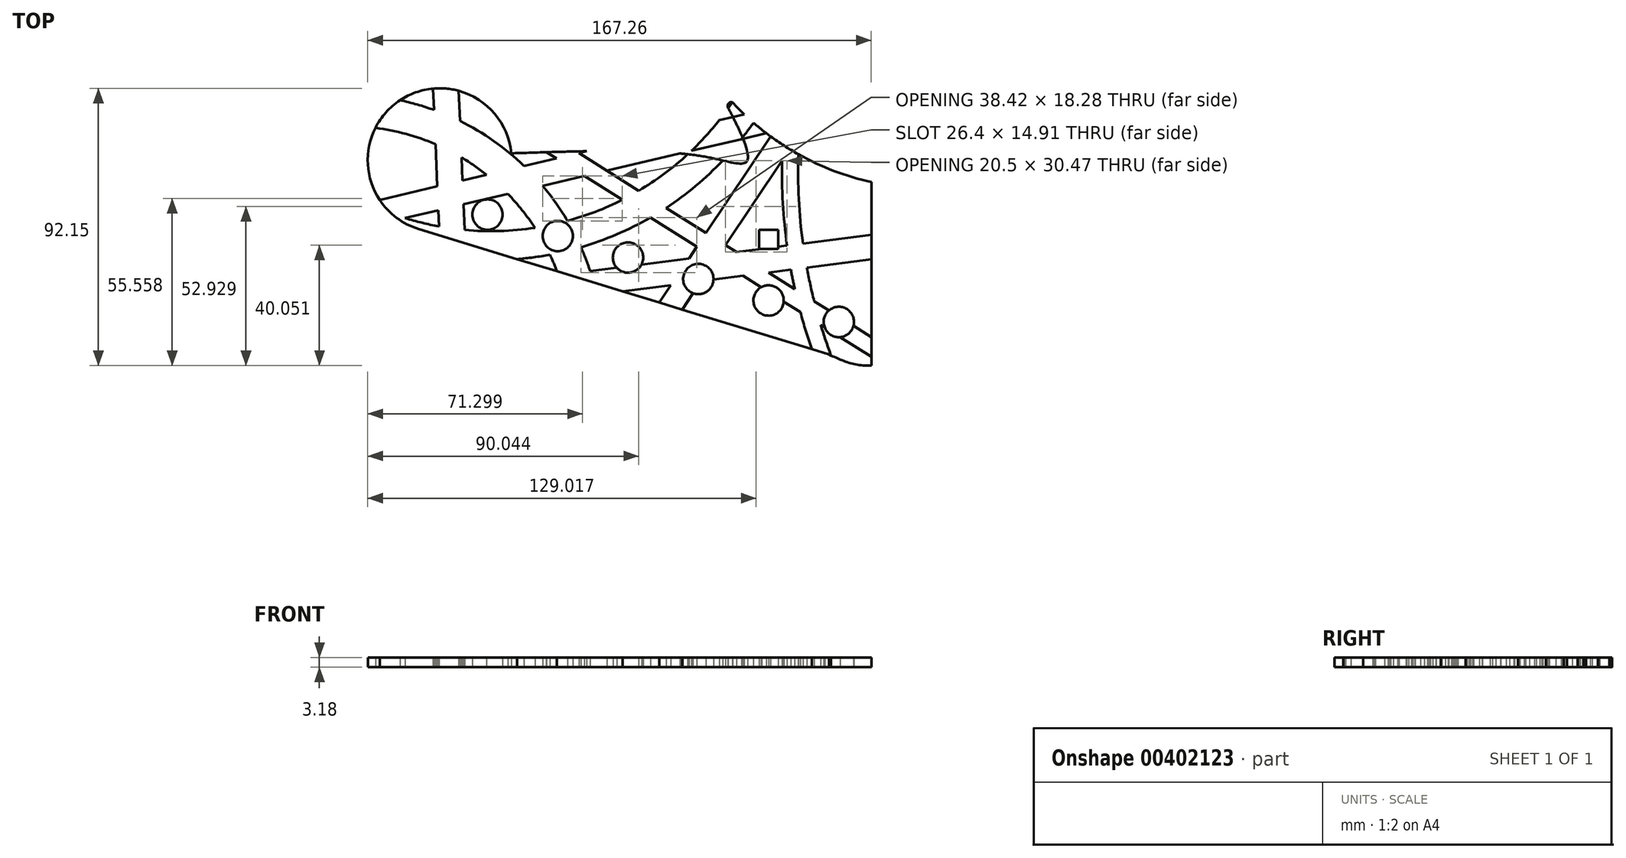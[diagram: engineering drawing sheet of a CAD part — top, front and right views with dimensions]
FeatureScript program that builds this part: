
annotation { "Feature Type Name" : "Feature", "Feature Type Description" : "" }
export const myFeature = defineFeature(function(context is Context, id is Id, definition is map)
    precondition{}
    {
        {
            var Q0;
            Q0=qCreatedBy(makeId("Top.planeOp"),FACE);
            var sketch = newSketch(context, id + "F0", { "sketchPlane" : qUnion([Q0])});
            skArc(sketch, "E0", {"start": v(-90.46, -15.28) * mm, "mid": v(-14.2, -9.68) * mm, "end": v(38.46, 45.77) * mm});
            skArc(sketch, "E1.0", {"start": v(-100.3, -1.2) * mm, "mid": v(-24.88, -3.77) * mm, "end": v(29.26, 48.8) * mm});
            skArc(sketch, "E2", {"start": v(51.31, 64.63) * mm, "mid": v(42.5, 3.49) * mm, "end": v(55.46, -56.9) * mm});
            skArc(sketch, "E3.0", {"start": v(46.25, 66.31) * mm, "mid": v(37.17, 3.3) * mm, "end": v(50.52, -58.93) * mm});
            skArc(sketch, "E4", {"start": v(-33.41, -40.98) * mm, "mid": v(-60.63, 8.15) * mm, "end": v(-114.4, 24.36) * mm});
            skArc(sketch, "E5.0", {"start": v(-23.07, -39.74) * mm, "mid": v(-54.1, 16.25) * mm, "end": v(-115.38, 34.73) * mm});
            skLineSegment(sketch, "E6.0", {"start": v(52.65, -51.2) * mm, "end": v(-83.61, -9.54) * mm});
            skArc(sketch, "E6.1", {"start": v(-52.83, 15.6) * mm, "mid": v(-91.75, 31.83) * mm, "end": v(-83.61, -9.54) * mm});
            skFitSpline(sketch, "E6.5", {"points": [v(52.65, -51.2) * mm, v(64.8, -54.91) * mm, v(80.38, -50.62) * mm, v(85.15, -44.27) * mm]});
            skLineSegment(sketch, "E6.6", {"start": v(66.1, 6.22) * mm, "end": v(66.1, -52.4) * mm});
            skPoint(sketch, "E7.visualSharp", {"position": v(13.9, 42.17) * mm});
            skArc(sketch, "E8", {"start": v(12.87, 42.18) * mm, "mid": v(44.36, 14.28) * mm, "end": v(85.15, 3.99) * mm});
            skFitSpline(sketch, "E9", {"points": [v(-52.83, 15.6) * mm, v(12.87, 42.18) * mm], "startDerivative": vector(194.61, -3.65) * mm, "endDerivative": vector(-37.72, 87.36) * mm});
            skLineSegment(sketch, "E10", {"start": v(66.73, 6.07) * mm, "end": v(66.73, -50.68) * mm});
            skLineSegment(sketch, "E11", {"start": v(66.73, -50.68) * mm, "end": v(66.73, -55.63) * mm});
            skArc(sketch, "E12", {"start": v(66.1, -52.4) * mm, "mid": v(66.43, -52.34) * mm, "end": v(66.73, -52.2) * mm});
            skSolve(sketch);
        }
        {
            var Q0;
            Q0=qCreatedBy(makeId("Top.planeOp"),FACE);
            var sketch = newSketch(context, id + "F1", { "sketchPlane" : qUnion([Q0])});
            skLineSegment(sketch, "E13", {"start": v(41.28, 19.45) * mm, "end": v(0, -42.12) * mm});
            skLineSegment(sketch, "E14", {"start": v(0, -42.12) * mm, "end": v(-6.32, -37.88) * mm});
            skLineSegment(sketch, "E15", {"start": v(-6.32, -37.88) * mm, "end": v(38.05, 28.32) * mm});
            skLineSegment(sketch, "E16", {"start": v(38.05, 28.32) * mm, "end": v(41.28, 19.45) * mm});
            skLineSegment(sketch, "E17", {"start": v(40.9, -75.03) * mm, "end": v(46.22, -72.68) * mm});
            skLineSegment(sketch, "E18", {"start": v(-56.42, -35.5) * mm, "end": v(132.52, -11.1) * mm});
            skLineSegment(sketch, "E19", {"start": v(132.52, -11.1) * mm, "end": v(131.24, -3.12) * mm});
            skLineSegment(sketch, "E20", {"start": v(131.24, -3.12) * mm, "end": v(-56.79, -27.4) * mm});
            skLineSegment(sketch, "E21", {"start": v(-56.79, -27.4) * mm, "end": v(-56.42, -35.5) * mm});
            skLineSegment(sketch, "E22", {"start": v(-71.95, 73.85) * mm, "end": v(-66.69, -48.5) * mm});
            skLineSegment(sketch, "E23", {"start": v(-66.69, -48.5) * mm, "end": v(-75.13, -48.86) * mm});
            skLineSegment(sketch, "E24", {"start": v(-75.13, -48.86) * mm, "end": v(-80.24, 69.83) * mm});
            skLineSegment(sketch, "E25", {"start": v(-80.24, 69.83) * mm, "end": v(-71.95, 73.85) * mm});
            skLineSegment(sketch, "E26", {"start": v(70.66, -54.45) * mm, "end": v(-45.44, 18.7) * mm});
            skLineSegment(sketch, "E27", {"start": v(-45.44, 18.7) * mm, "end": v(-42.5, 23.35) * mm});
            skLineSegment(sketch, "E28", {"start": v(-42.5, 23.35) * mm, "end": v(73.52, -49.75) * mm});
            skLineSegment(sketch, "E29", {"start": v(73.52, -49.75) * mm, "end": v(70.66, -54.45) * mm});
            skLineSegment(sketch, "E30", {"start": v(56.6, 28.12) * mm, "end": v(-113.4, -11.85) * mm});
            skLineSegment(sketch, "E31", {"start": v(-113.4, -11.85) * mm, "end": v(-115.19, -4.23) * mm});
            skLineSegment(sketch, "E32", {"start": v(-115.19, -4.23) * mm, "end": v(55.1, 35.8) * mm});
            skLineSegment(sketch, "E33", {"start": v(55.1, 35.8) * mm, "end": v(56.6, 28.12) * mm});
            skArc(sketch, "E34.0", {"start": v(-90.46, -15.28) * mm, "mid": v(-14.2, -9.68) * mm, "end": v(38.46, 45.77) * mm});
            skArc(sketch, "E34.1", {"start": v(-100.3, -1.2) * mm, "mid": v(-24.88, -3.77) * mm, "end": v(29.26, 48.8) * mm});
            skArc(sketch, "E34.2", {"start": v(51.31, 64.63) * mm, "mid": v(42.5, 3.49) * mm, "end": v(55.46, -56.9) * mm});
            skArc(sketch, "E34.3", {"start": v(46.25, 66.31) * mm, "mid": v(37.17, 3.3) * mm, "end": v(50.52, -58.93) * mm});
            skArc(sketch, "E34.4", {"start": v(-33.41, -40.98) * mm, "mid": v(-60.63, 8.15) * mm, "end": v(-114.4, 24.36) * mm});
            skArc(sketch, "E34.5", {"start": v(-23.07, -39.74) * mm, "mid": v(-54.1, 16.25) * mm, "end": v(-115.38, 34.73) * mm});
            skArc(sketch, "E35.0", {"start": v(-52.83, 15.6) * mm, "mid": v(-91.75, 31.83) * mm, "end": v(-83.61, -9.54) * mm});
            skFitSpline(sketch, "E35.1", {"points": [v(-52.83, 15.6) * mm, v(12.04, 14.39) * mm, v(25.44, 13.06) * mm, v(12.87, 42.18) * mm]});
            skArc(sketch, "E35.2", {"start": v(12.87, 42.18) * mm, "mid": v(44.36, 14.28) * mm, "end": v(85.15, 3.99) * mm});
            skLineSegment(sketch, "E35.3", {"start": v(66.1, 6.22) * mm, "end": v(66.1, -52.4) * mm});
            skFitSpline(sketch, "E35.4", {"points": [v(52.65, -51.2) * mm, v(64.8, -54.91) * mm, v(80.38, -50.62) * mm, v(85.15, -44.27) * mm]});
            skLineSegment(sketch, "E35.5", {"start": v(52.65, -51.2) * mm, "end": v(-83.61, -9.54) * mm});
            skLineSegment(sketch, "E36.0", {"start": v(66.73, 6.07) * mm, "end": v(66.73, -50.68) * mm});
            skLineSegment(sketch, "E37.0", {"start": v(66.73, -50.68) * mm, "end": v(66.73, -55.63) * mm});
            skArc(sketch, "E38.0", {"start": v(66.1, -52.4) * mm, "mid": v(66.43, -52.34) * mm, "end": v(66.73, -52.2) * mm});
            skSolve(sketch);
        }
        {
            var Q0;
            {var subQ0=sQuery(id+"F1.wireOp",EDGE,"E35.3");var subQ1=sQuery(id+"F1.wireOp",EDGE,"E26");var subQ2=makeQuery(id+"F1.imprint","INTERSECT",VERTEX,{"derivedFrom":[subQ1,subQ0]});Q0=makeQuery(id+"F1.imprint","IMPRINT",FACE,{"disambiguationData":[TD([[makeQuery(id+"F1.imprint","IMPRINT",EDGE,{"disambiguationData":[TD([[subQ2,-1.0]])],"derivedFrom":subQ1}),-1.0]])]});}
            var Q1;
            {var subQ0=sQuery(id+"F1.wireOp",EDGE,"E37.0");var subQ6=sQuery(id+"F1.wireOp",EDGE,"E26");var subQ9=makeQuery(id+"F1.imprint","INTERSECT",VERTEX,{"derivedFrom":[subQ6,subQ0]});Q1=makeQuery(id+"F1.imprint","IMPRINT",FACE,{"disambiguationData":[TD([[makeQuery(id+"F1.imprint","IMPRINT",EDGE,{"disambiguationData":[TD([[subQ9,-1.0]])],"derivedFrom":subQ6}),-1.0]])]});}
            var Q2;
            {var subQ0=sQuery(id+"F1.wireOp",EDGE,"E36.0");var subQ1=sQuery(id+"F1.wireOp",EDGE,"E18");var subQ2=makeQuery(id+"F1.imprint","INTERSECT",VERTEX,{"derivedFrom":[subQ1,subQ0]});Q2=makeQuery(id+"F1.imprint","IMPRINT",FACE,{"disambiguationData":[TD([[makeQuery(id+"F1.imprint","IMPRINT",EDGE,{"disambiguationData":[TD([[subQ2,1.0]])],"derivedFrom":subQ1}),1.0]])]});}
            var Q3;
            {var subQ0=sQuery(id+"F1.wireOp",EDGE,"E34.2");var subQ1=sQuery(id+"F1.wireOp",EDGE,"E18");var subQ2=makeQuery(id+"F1.imprint","INTERSECT",VERTEX,{"derivedFrom":[subQ1,subQ0]});Q3=makeQuery(id+"F1.imprint","IMPRINT",FACE,{"disambiguationData":[TD([[makeQuery(id+"F1.imprint","IMPRINT",EDGE,{"disambiguationData":[TD([[subQ2,-1.0]])],"derivedFrom":subQ1}),1.0]])]});}
            var Q4;
            {var subQ0=sQuery(id+"F1.wireOp",EDGE,"E34.2");var subQ1=sQuery(id+"F1.wireOp",EDGE,"E13");var subQ2=makeQuery(id+"F1.imprint","INTERSECT",VERTEX,{"derivedFrom":[subQ1,subQ0]});Q4=makeQuery(id+"F1.imprint","IMPRINT",FACE,{"disambiguationData":[TD([[makeQuery(id+"F1.imprint","IMPRINT",EDGE,{"disambiguationData":[TD([[subQ2,-1.0]])],"derivedFrom":subQ1}),-1.0]])]});}
            var Q5;
            {var subQ0=sQuery(id+"F1.wireOp",EDGE,"E34.3");var subQ1=sQuery(id+"F1.wireOp",EDGE,"E13");var subQ2=makeQuery(id+"F1.imprint","INTERSECT",VERTEX,{"derivedFrom":[subQ1,subQ0]});Q5=makeQuery(id+"F1.imprint","IMPRINT",FACE,{"disambiguationData":[TD([[makeQuery(id+"F1.imprint","IMPRINT",EDGE,{"disambiguationData":[TD([[subQ2,-1.0]])],"derivedFrom":subQ1}),-1.0]])]});}
            var Q6;
            {var subQ0=sQuery(id+"F1.wireOp",EDGE,"E34.2");var subQ1=sQuery(id+"F1.wireOp",EDGE,"E13");var subQ2=makeQuery(id+"F1.imprint","INTERSECT",VERTEX,{"derivedFrom":[subQ1,subQ0]});Q6=makeQuery(id+"F1.imprint","IMPRINT",FACE,{"disambiguationData":[TD([[makeQuery(id+"F1.imprint","IMPRINT",EDGE,{"disambiguationData":[TD([[subQ2,-1.0]])],"derivedFrom":subQ1}),1.0]])]});}
            var Q7;
            {var subQ0=sQuery(id+"F1.wireOp",EDGE,"E34.3");var subQ1=sQuery(id+"F1.wireOp",EDGE,"E18");var subQ2=makeQuery(id+"F1.imprint","INTERSECT",VERTEX,{"derivedFrom":[subQ1,subQ0]});Q7=makeQuery(id+"F1.imprint","IMPRINT",FACE,{"disambiguationData":[TD([[makeQuery(id+"F1.imprint","IMPRINT",EDGE,{"disambiguationData":[TD([[subQ2,-1.0]])],"derivedFrom":subQ1}),1.0]])]});}
            var Q8;
            {var subQ0=sQuery(id+"F1.wireOp",EDGE,"E34.3");var subQ1=sQuery(id+"F1.wireOp",EDGE,"E18");var subQ2=makeQuery(id+"F1.imprint","INTERSECT",VERTEX,{"derivedFrom":[subQ1,subQ0]});Q8=makeQuery(id+"F1.imprint","IMPRINT",FACE,{"disambiguationData":[TD([[makeQuery(id+"F1.imprint","IMPRINT",EDGE,{"disambiguationData":[TD([[subQ2,-1.0]])],"derivedFrom":subQ1}),-1.0]])]});}
            var Q9;
            {var subQ0=sQuery(id+"F1.wireOp",EDGE,"E34.2");var subQ1=sQuery(id+"F1.wireOp",EDGE,"E26");var subQ2=makeQuery(id+"F1.imprint","INTERSECT",VERTEX,{"derivedFrom":[subQ1,subQ0]});Q9=makeQuery(id+"F1.imprint","IMPRINT",FACE,{"disambiguationData":[TD([[makeQuery(id+"F1.imprint","IMPRINT",EDGE,{"disambiguationData":[TD([[subQ2,-1.0]])],"derivedFrom":subQ1}),-1.0]])]});}
            var Q10;
            {var subQ3=sQuery(id+"F1.wireOp",EDGE,"E34.2");var subQ7=sQuery(id+"F1.wireOp",EDGE,"E26");var subQ9=makeQuery(id+"F1.imprint","INTERSECT",VERTEX,{"derivedFrom":[subQ7,subQ3]});Q10=makeQuery(id+"F1.imprint","IMPRINT",FACE,{"disambiguationData":[TD([[makeQuery(id+"F1.imprint","IMPRINT",EDGE,{"disambiguationData":[TD([[subQ9,-1.0]])],"derivedFrom":subQ7}),1.0]])]});}
            var Q11;
            {var subQ0=sQuery(id+"F1.wireOp",EDGE,"E26");var subQ1=sQuery(id+"F1.wireOp",EDGE,"E18");var subQ2=makeQuery(id+"F1.imprint","INTERSECT",VERTEX,{"derivedFrom":[subQ1,subQ0]});Q11=makeQuery(id+"F1.imprint","IMPRINT",FACE,{"disambiguationData":[TD([[makeQuery(id+"F1.imprint","IMPRINT",EDGE,{"disambiguationData":[TD([[subQ2,-1.0]])],"derivedFrom":subQ1}),-1.0]])]});}
            var Q12;
            {var subQ0=sQuery(id+"F1.wireOp",EDGE,"E28");var subQ1=sQuery(id+"F1.wireOp",EDGE,"E18");var subQ2=makeQuery(id+"F1.imprint","INTERSECT",VERTEX,{"derivedFrom":[subQ1,subQ0]});Q12=makeQuery(id+"F1.imprint","IMPRINT",FACE,{"disambiguationData":[TD([[makeQuery(id+"F1.imprint","IMPRINT",EDGE,{"disambiguationData":[TD([[subQ2,-1.0]])],"derivedFrom":subQ1}),1.0]])]});}
            var Q13;
            {var subQ0=sQuery(id+"F1.wireOp",EDGE,"E20");var subQ1=sQuery(id+"F1.wireOp",EDGE,"E13");var subQ2=makeQuery(id+"F1.imprint","INTERSECT",VERTEX,{"derivedFrom":[subQ1,subQ0]});Q13=makeQuery(id+"F1.imprint","IMPRINT",FACE,{"disambiguationData":[TD([[makeQuery(id+"F1.imprint","IMPRINT",EDGE,{"disambiguationData":[TD([[subQ2,-1.0]])],"derivedFrom":subQ1}),1.0]])]});}
            var Q14;
            {var subQ0=sQuery(id+"F1.wireOp",EDGE,"E28");var subQ1=sQuery(id+"F1.wireOp",EDGE,"E13");var subQ2=makeQuery(id+"F1.imprint","INTERSECT",VERTEX,{"derivedFrom":[subQ1,subQ0]});Q14=makeQuery(id+"F1.imprint","IMPRINT",FACE,{"disambiguationData":[TD([[makeQuery(id+"F1.imprint","IMPRINT",EDGE,{"disambiguationData":[TD([[subQ2,-1.0]])],"derivedFrom":subQ1}),1.0]])]});}
            var Q15;
            {var subQ1=sQuery(id+"F1.wireOp",EDGE,"E13");var subQ7=sQuery(id+"F1.wireOp",EDGE,"E28");var subQ9=makeQuery(id+"F1.imprint","INTERSECT",VERTEX,{"derivedFrom":[subQ1,subQ7]});Q15=makeQuery(id+"F1.imprint","IMPRINT",FACE,{"disambiguationData":[TD([[makeQuery(id+"F1.imprint","IMPRINT",EDGE,{"disambiguationData":[TD([[subQ9,-1.0]])],"derivedFrom":subQ1}),-1.0]])]});}
            var Q16;
            {var subQ0=sQuery(id+"F1.wireOp",EDGE,"E26");var subQ1=sQuery(id+"F1.wireOp",EDGE,"E13");var subQ2=makeQuery(id+"F1.imprint","INTERSECT",VERTEX,{"derivedFrom":[subQ1,subQ0]});Q16=makeQuery(id+"F1.imprint","IMPRINT",FACE,{"disambiguationData":[TD([[makeQuery(id+"F1.imprint","IMPRINT",EDGE,{"disambiguationData":[TD([[subQ2,-1.0]])],"derivedFrom":subQ1}),1.0]])]});}
            var Q17;
            {var subQ0=sQuery(id+"F1.wireOp",EDGE,"E20");var subQ1=sQuery(id+"F1.wireOp",EDGE,"E13");var subQ2=makeQuery(id+"F1.imprint","INTERSECT",VERTEX,{"derivedFrom":[subQ1,subQ0]});Q17=makeQuery(id+"F1.imprint","IMPRINT",FACE,{"disambiguationData":[TD([[makeQuery(id+"F1.imprint","IMPRINT",EDGE,{"disambiguationData":[TD([[subQ2,-1.0]])],"derivedFrom":subQ1}),-1.0]])]});}
            var Q18;
            {var subQ1=sQuery(id+"F1.wireOp",EDGE,"E13");var subQ7=sQuery(id+"F1.wireOp",EDGE,"E26");var subQ9=makeQuery(id+"F1.imprint","INTERSECT",VERTEX,{"derivedFrom":[subQ1,subQ7]});Q18=makeQuery(id+"F1.imprint","IMPRINT",FACE,{"disambiguationData":[TD([[makeQuery(id+"F1.imprint","IMPRINT",EDGE,{"disambiguationData":[TD([[subQ9,-1.0]])],"derivedFrom":subQ1}),-1.0]])]});}
            var Q19;
            {var subQ0=sQuery(id+"F1.wireOp",EDGE,"E20");var subQ1=sQuery(id+"F1.wireOp",EDGE,"E15");var subQ2=makeQuery(id+"F1.imprint","INTERSECT",VERTEX,{"derivedFrom":[subQ1,subQ0]});Q19=makeQuery(id+"F1.imprint","IMPRINT",FACE,{"disambiguationData":[TD([[makeQuery(id+"F1.imprint","IMPRINT",EDGE,{"disambiguationData":[TD([[subQ2,-1.0]])],"derivedFrom":subQ1}),-1.0]])]});}
            var Q20;
            {var subQ0=sQuery(id+"F1.wireOp",EDGE,"E35.5");var subQ1=sQuery(id+"F1.wireOp",EDGE,"E13");var subQ2=makeQuery(id+"F1.imprint","INTERSECT",VERTEX,{"derivedFrom":[subQ1,subQ0]});Q20=makeQuery(id+"F1.imprint","IMPRINT",FACE,{"disambiguationData":[TD([[makeQuery(id+"F1.imprint","IMPRINT",EDGE,{"disambiguationData":[TD([[subQ2,1.0]])],"derivedFrom":subQ1}),-1.0]])]});}
            var Q21;
            {var subQ1=sQuery(id+"F1.wireOp",EDGE,"E18");var subQ3=sQuery(id+"F1.wireOp",EDGE,"E15");var subQ4=makeQuery(id+"F1.imprint","INTERSECT",VERTEX,{"derivedFrom":[subQ3,subQ1]});Q21=makeQuery(id+"F1.imprint","IMPRINT",FACE,{"disambiguationData":[TD([[makeQuery(id+"F1.imprint","IMPRINT",EDGE,{"disambiguationData":[TD([[subQ4,-1.0]])],"derivedFrom":subQ3}),1.0]])]});}
            var Q22;
            {var subQ0=sQuery(id+"F1.wireOp",EDGE,"E26");var subQ1=sQuery(id+"F1.wireOp",EDGE,"E15");var subQ2=makeQuery(id+"F1.imprint","INTERSECT",VERTEX,{"derivedFrom":[subQ1,subQ0]});Q22=makeQuery(id+"F1.imprint","IMPRINT",FACE,{"disambiguationData":[TD([[makeQuery(id+"F1.imprint","IMPRINT",EDGE,{"disambiguationData":[TD([[subQ2,-1.0]])],"derivedFrom":subQ1}),1.0]])]});}
            var Q23;
            {var subQ0=sQuery(id+"F1.wireOp",EDGE,"E34.1");var subQ1=sQuery(id+"F1.wireOp",EDGE,"E28");var subQ2=makeQuery(id+"F1.imprint","INTERSECT",VERTEX,{"derivedFrom":[subQ1,subQ0]});Q23=makeQuery(id+"F1.imprint","IMPRINT",FACE,{"disambiguationData":[TD([[makeQuery(id+"F1.imprint","IMPRINT",EDGE,{"disambiguationData":[TD([[subQ2,-1.0]])],"derivedFrom":subQ1}),1.0]])]});}
            var Q24;
            {var subQ1=sQuery(id+"F1.wireOp",EDGE,"E30");var subQ9=sQuery(id+"F1.wireOp",EDGE,"E34.0");var subQ10=makeQuery(id+"F1.imprint","INTERSECT",VERTEX,{"derivedFrom":[subQ1,subQ9]});Q24=makeQuery(id+"F1.imprint","IMPRINT",FACE,{"disambiguationData":[TD([[makeQuery(id+"F1.imprint","IMPRINT",EDGE,{"disambiguationData":[TD([[subQ10,-1.0]])],"derivedFrom":subQ1}),-1.0]])]});}
            var Q25;
            {var subQ0=sQuery(id+"F1.wireOp",EDGE,"E35.2");var subQ1=sQuery(id+"F1.wireOp",EDGE,"E32");var subQ2=makeQuery(id+"F1.imprint","INTERSECT",VERTEX,{"derivedFrom":[subQ1,subQ0]});Q25=makeQuery(id+"F1.imprint","IMPRINT",FACE,{"disambiguationData":[TD([[makeQuery(id+"F1.imprint","IMPRINT",EDGE,{"disambiguationData":[TD([[subQ2,1.0]])],"derivedFrom":subQ1}),1.0]])]});}
            var Q26;
            {var subQ0=sQuery(id+"F1.wireOp",EDGE,"E35.1");var subQ1=sQuery(id+"F1.wireOp",EDGE,"E28");var subQ2=makeQuery(id+"F1.imprint","INTERSECT",VERTEX,{"derivedFrom":[subQ1,subQ0]});Q26=makeQuery(id+"F1.imprint","IMPRINT",FACE,{"disambiguationData":[TD([[makeQuery(id+"F1.imprint","IMPRINT",EDGE,{"disambiguationData":[TD([[subQ2,-1.0]])],"derivedFrom":subQ1}),1.0]])]});}
            var Q27;
            {var subQ0=sQuery(id+"F1.wireOp",EDGE,"E34.0");var subQ1=sQuery(id+"F1.wireOp",EDGE,"E26");var subQ2=makeQuery(id+"F1.imprint","INTERSECT",VERTEX,{"derivedFrom":[subQ1,subQ0]});Q27=makeQuery(id+"F1.imprint","IMPRINT",FACE,{"disambiguationData":[TD([[makeQuery(id+"F1.imprint","IMPRINT",EDGE,{"disambiguationData":[TD([[subQ2,-1.0]])],"derivedFrom":subQ1}),-1.0]])]});}
            var Q28;
            {var subQ0=sQuery(id+"F1.wireOp",EDGE,"E34.1");var subQ1=sQuery(id+"F1.wireOp",EDGE,"E26");var subQ2=makeQuery(id+"F1.imprint","INTERSECT",VERTEX,{"derivedFrom":[subQ1,subQ0]});Q28=makeQuery(id+"F1.imprint","IMPRINT",FACE,{"disambiguationData":[TD([[makeQuery(id+"F1.imprint","IMPRINT",EDGE,{"disambiguationData":[TD([[subQ2,-1.0]])],"derivedFrom":subQ1}),-1.0]])]});}
            var Q29;
            {var subQ0=sQuery(id+"F1.wireOp",EDGE,"E30");var subQ1=sQuery(id+"F1.wireOp",EDGE,"E26");var subQ2=makeQuery(id+"F1.imprint","INTERSECT",VERTEX,{"derivedFrom":[subQ1,subQ0]});Q29=makeQuery(id+"F1.imprint","IMPRINT",FACE,{"disambiguationData":[TD([[makeQuery(id+"F1.imprint","IMPRINT",EDGE,{"disambiguationData":[TD([[subQ2,-1.0]])],"derivedFrom":subQ1}),-1.0]])]});}
            var Q30;
            {var subQ0=sQuery(id+"F1.wireOp",EDGE,"E35.1");var subQ1=sQuery(id+"F1.wireOp",EDGE,"E26");var subQ2=makeQuery(id+"F1.imprint","INTERSECT",VERTEX,{"derivedFrom":[subQ1,subQ0]});Q30=makeQuery(id+"F1.imprint","IMPRINT",FACE,{"disambiguationData":[TD([[makeQuery(id+"F1.imprint","IMPRINT",EDGE,{"disambiguationData":[TD([[subQ2,1.0]])],"derivedFrom":subQ1}),-1.0]])]});}
            var Q31;
            {var subQ0=sQuery(id+"F1.wireOp",EDGE,"E30");var subQ1=sQuery(id+"F1.wireOp",EDGE,"E26");var subQ2=makeQuery(id+"F1.imprint","INTERSECT",VERTEX,{"derivedFrom":[subQ1,subQ0]});Q31=makeQuery(id+"F1.imprint","IMPRINT",FACE,{"disambiguationData":[TD([[makeQuery(id+"F1.imprint","IMPRINT",EDGE,{"disambiguationData":[TD([[subQ2,-1.0]])],"derivedFrom":subQ1}),1.0]])]});}
            var Q32;
            {var subQ0=sQuery(id+"F1.wireOp",EDGE,"E34.0");var subQ1=sQuery(id+"F1.wireOp",EDGE,"E26");var subQ2=makeQuery(id+"F1.imprint","INTERSECT",VERTEX,{"derivedFrom":[subQ1,subQ0]});Q32=makeQuery(id+"F1.imprint","IMPRINT",FACE,{"disambiguationData":[TD([[makeQuery(id+"F1.imprint","IMPRINT",EDGE,{"disambiguationData":[TD([[subQ2,-1.0]])],"derivedFrom":subQ1}),1.0]])]});}
            var Q33;
            {var subQ0=sQuery(id+"F1.wireOp",EDGE,"E34.5");var subQ1=sQuery(id+"F1.wireOp",EDGE,"E20");var subQ2=makeQuery(id+"F1.imprint","INTERSECT",VERTEX,{"derivedFrom":[subQ1,subQ0]});Q33=makeQuery(id+"F1.imprint","IMPRINT",FACE,{"disambiguationData":[TD([[makeQuery(id+"F1.imprint","IMPRINT",EDGE,{"disambiguationData":[TD([[subQ2,-1.0]])],"derivedFrom":subQ1}),1.0]])]});}
            var Q34;
            {var subQ5=sQuery(id+"F1.wireOp",EDGE,"E34.5");var subQ7=sQuery(id+"F1.wireOp",EDGE,"E20");var subQ8=makeQuery(id+"F1.imprint","INTERSECT",VERTEX,{"derivedFrom":[subQ7,subQ5]});Q34=makeQuery(id+"F1.imprint","IMPRINT",FACE,{"disambiguationData":[TD([[makeQuery(id+"F1.imprint","IMPRINT",EDGE,{"disambiguationData":[TD([[subQ8,-1.0]])],"derivedFrom":subQ7}),-1.0]])]});}
            var Q35;
            {var subQ0=sQuery(id+"F1.wireOp",EDGE,"E34.4");var subQ1=sQuery(id+"F1.wireOp",EDGE,"E34.0");var subQ2=makeQuery(id+"F1.imprint","INTERSECT",VERTEX,{"derivedFrom":[subQ1,subQ0]});Q35=makeQuery(id+"F1.imprint","IMPRINT",FACE,{"disambiguationData":[TD([[makeQuery(id+"F1.imprint","IMPRINT",EDGE,{"disambiguationData":[TD([[subQ2,-1.0]])],"derivedFrom":subQ1}),1.0]])]});}
            var Q36;
            {var subQ0=sQuery(id+"F1.wireOp",EDGE,"E34.5");var subQ1=sQuery(id+"F1.wireOp",EDGE,"E30");var subQ2=makeQuery(id+"F1.imprint","INTERSECT",VERTEX,{"derivedFrom":[subQ1,subQ0]});Q36=makeQuery(id+"F1.imprint","IMPRINT",FACE,{"disambiguationData":[TD([[makeQuery(id+"F1.imprint","IMPRINT",EDGE,{"disambiguationData":[TD([[subQ2,-1.0]])],"derivedFrom":subQ1}),1.0]])]});}
            var Q37;
            {var subQ0=sQuery(id+"F1.wireOp",EDGE,"E34.5");var subQ1=sQuery(id+"F1.wireOp",EDGE,"E30");var subQ2=makeQuery(id+"F1.imprint","INTERSECT",VERTEX,{"derivedFrom":[subQ1,subQ0]});Q37=makeQuery(id+"F1.imprint","IMPRINT",FACE,{"disambiguationData":[TD([[makeQuery(id+"F1.imprint","IMPRINT",EDGE,{"disambiguationData":[TD([[subQ2,-1.0]])],"derivedFrom":subQ1}),-1.0]])]});}
            var Q38;
            {var subQ0=sQuery(id+"F1.wireOp",EDGE,"E34.5");var subQ1=sQuery(id+"F1.wireOp",EDGE,"E22");var subQ2=makeQuery(id+"F1.imprint","INTERSECT",VERTEX,{"derivedFrom":[subQ1,subQ0]});Q38=makeQuery(id+"F1.imprint","IMPRINT",FACE,{"disambiguationData":[TD([[makeQuery(id+"F1.imprint","IMPRINT",EDGE,{"disambiguationData":[TD([[subQ2,-1.0]])],"derivedFrom":subQ1}),1.0]])]});}
            var Q39;
            {var subQ0=sQuery(id+"F1.wireOp",EDGE,"E34.5");var subQ1=sQuery(id+"F1.wireOp",EDGE,"E22");var subQ2=makeQuery(id+"F1.imprint","INTERSECT",VERTEX,{"derivedFrom":[subQ1,subQ0]});Q39=makeQuery(id+"F1.imprint","IMPRINT",FACE,{"disambiguationData":[TD([[makeQuery(id+"F1.imprint","IMPRINT",EDGE,{"disambiguationData":[TD([[subQ2,-1.0]])],"derivedFrom":subQ1}),-1.0]])]});}
            var Q40;
            {var subQ0=sQuery(id+"F1.wireOp",EDGE,"E35.0");var subQ1=sQuery(id+"F1.wireOp",EDGE,"E22");var subQ2=makeQuery(id+"F1.imprint","INTERSECT",VERTEX,{"derivedFrom":[subQ1,subQ0]});Q40=makeQuery(id+"F1.imprint","IMPRINT",FACE,{"disambiguationData":[TD([[makeQuery(id+"F1.imprint","IMPRINT",EDGE,{"disambiguationData":[TD([[subQ2,-1.0]])],"derivedFrom":subQ1}),-1.0]])]});}
            var Q41;
            {var subQ0=sQuery(id+"F1.wireOp",EDGE,"E34.4");var subQ1=sQuery(id+"F1.wireOp",EDGE,"E24");var subQ2=makeQuery(id+"F1.imprint","INTERSECT",VERTEX,{"derivedFrom":[subQ1,subQ0]});Q41=makeQuery(id+"F1.imprint","IMPRINT",FACE,{"disambiguationData":[TD([[makeQuery(id+"F1.imprint","IMPRINT",EDGE,{"disambiguationData":[TD([[subQ2,-1.0]])],"derivedFrom":subQ1}),1.0]])]});}
            var Q42;
            {var subQ0=sQuery(id+"F1.wireOp",EDGE,"E34.4");var subQ1=sQuery(id+"F1.wireOp",EDGE,"E22");var subQ2=makeQuery(id+"F1.imprint","INTERSECT",VERTEX,{"derivedFrom":[subQ1,subQ0]});Q42=makeQuery(id+"F1.imprint","IMPRINT",FACE,{"disambiguationData":[TD([[makeQuery(id+"F1.imprint","IMPRINT",EDGE,{"disambiguationData":[TD([[subQ2,-1.0]])],"derivedFrom":subQ1}),-1.0]])]});}
            var Q43;
            {var subQ0=sQuery(id+"F1.wireOp",EDGE,"E30");var subQ1=sQuery(id+"F1.wireOp",EDGE,"E24");var subQ2=makeQuery(id+"F1.imprint","INTERSECT",VERTEX,{"derivedFrom":[subQ1,subQ0]});Q43=makeQuery(id+"F1.imprint","IMPRINT",FACE,{"disambiguationData":[TD([[makeQuery(id+"F1.imprint","IMPRINT",EDGE,{"disambiguationData":[TD([[subQ2,-1.0]])],"derivedFrom":subQ1}),1.0]])]});}
            var Q44;
            {var subQ0=sQuery(id+"F1.wireOp",EDGE,"E32");var subQ1=sQuery(id+"F1.wireOp",EDGE,"E22");var subQ2=makeQuery(id+"F1.imprint","INTERSECT",VERTEX,{"derivedFrom":[subQ1,subQ0]});Q44=makeQuery(id+"F1.imprint","IMPRINT",FACE,{"disambiguationData":[TD([[makeQuery(id+"F1.imprint","IMPRINT",EDGE,{"disambiguationData":[TD([[subQ2,-1.0]])],"derivedFrom":subQ1}),-1.0]])]});}
            var Q45;
            {var subQ0=sQuery(id+"F1.wireOp",EDGE,"E32");var subQ1=sQuery(id+"F1.wireOp",EDGE,"E22");var subQ2=makeQuery(id+"F1.imprint","INTERSECT",VERTEX,{"derivedFrom":[subQ1,subQ0]});Q45=makeQuery(id+"F1.imprint","IMPRINT",FACE,{"disambiguationData":[TD([[makeQuery(id+"F1.imprint","IMPRINT",EDGE,{"disambiguationData":[TD([[subQ2,-1.0]])],"derivedFrom":subQ1}),1.0]])]});}
            var Q46;
            {var subQ0=sQuery(id+"F1.wireOp",EDGE,"E30");var subQ1=sQuery(id+"F1.wireOp",EDGE,"E22");var subQ2=makeQuery(id+"F1.imprint","INTERSECT",VERTEX,{"derivedFrom":[subQ1,subQ0]});Q46=makeQuery(id+"F1.imprint","IMPRINT",FACE,{"disambiguationData":[TD([[makeQuery(id+"F1.imprint","IMPRINT",EDGE,{"disambiguationData":[TD([[subQ2,-1.0]])],"derivedFrom":subQ1}),-1.0]])]});}
            var Q47;
            {var subQ0=sQuery(id+"F1.wireOp",EDGE,"E35.5");var subQ1=sQuery(id+"F1.wireOp",EDGE,"E34.0");var subQ2=makeQuery(id+"F1.imprint","INTERSECT",VERTEX,{"derivedFrom":[subQ1,subQ0]});Q47=makeQuery(id+"F1.imprint","IMPRINT",FACE,{"disambiguationData":[TD([[makeQuery(id+"F1.imprint","IMPRINT",EDGE,{"disambiguationData":[TD([[subQ2,-1.0]])],"derivedFrom":subQ1}),1.0]])]});}
            var Q48;
            {var subQ1=sQuery(id+"F1.wireOp",EDGE,"E13");var subQ5=sQuery(id+"F1.wireOp",EDGE,"E35.2");var subQ8=makeQuery(id+"F1.imprint","INTERSECT",VERTEX,{"derivedFrom":[subQ1,subQ5]});Q48=makeQuery(id+"F1.imprint","IMPRINT",FACE,{"disambiguationData":[TD([[makeQuery(id+"F1.imprint","IMPRINT",EDGE,{"disambiguationData":[TD([[subQ8,-1.0]])],"derivedFrom":subQ1}),1.0]])]});}
            var Q49;
            {var subQ0=sQuery(id+"F1.wireOp",EDGE,"E35.2");var subQ1=sQuery(id+"F1.wireOp",EDGE,"E30");var subQ2=makeQuery(id+"F1.imprint","INTERSECT",VERTEX,{"derivedFrom":[subQ1,subQ0]});Q49=makeQuery(id+"F1.imprint","IMPRINT",FACE,{"disambiguationData":[TD([[makeQuery(id+"F1.imprint","IMPRINT",EDGE,{"disambiguationData":[TD([[subQ2,-1.0]])],"derivedFrom":subQ1}),-1.0]])]});}
            var Q50;
            {var subQ0=sQuery(id+"F1.wireOp",EDGE,"E34.1");var subQ1=sQuery(id+"F1.wireOp",EDGE,"E22");var subQ2=makeQuery(id+"F1.imprint","INTERSECT",VERTEX,{"derivedFrom":[subQ1,subQ0]});Q50=makeQuery(id+"F1.imprint","IMPRINT",FACE,{"disambiguationData":[TD([[makeQuery(id+"F1.imprint","IMPRINT",EDGE,{"disambiguationData":[TD([[subQ2,-1.0]])],"derivedFrom":subQ1}),-1.0]])]});}
            var Q51;
            {var subQ0=sQuery(id+"F1.wireOp",EDGE,"E35.5");var subQ6=sQuery(id+"F1.wireOp",EDGE,"E24");var subQ9=makeQuery(id+"F1.imprint","INTERSECT",VERTEX,{"derivedFrom":[subQ6,subQ0]});Q51=makeQuery(id+"F1.imprint","IMPRINT",FACE,{"disambiguationData":[TD([[makeQuery(id+"F1.imprint","IMPRINT",EDGE,{"disambiguationData":[TD([[subQ9,-1.0]])],"derivedFrom":subQ6}),1.0]])]});}
            var Q52;
            {var subQ0=sQuery(id+"F1.wireOp",EDGE,"E35.0");var subQ1=sQuery(id+"F1.wireOp",EDGE,"E30");var subQ2=makeQuery(id+"F1.imprint","INTERSECT",VERTEX,{"derivedFrom":[subQ1,subQ0]});Q52=makeQuery(id+"F1.imprint","IMPRINT",FACE,{"disambiguationData":[TD([[makeQuery(id+"F1.imprint","IMPRINT",EDGE,{"disambiguationData":[TD([[subQ2,1.0]])],"derivedFrom":subQ1}),-1.0]])]});}
            extrude(context, id + "F2", {"entities" : qUnion([Q0, Q1, Q2, Q3, Q4, Q5, Q6, Q7, Q8, Q9, Q10, Q11, Q12, Q13, Q14, Q15, Q16, Q17, Q18, Q19, Q20, Q21, Q22, Q23, Q24, Q25, Q26, Q27, Q28, Q29, Q30, Q31, Q32, Q33, Q34, Q35, Q36, Q37, Q38, Q39, Q40, Q41, Q42, Q43, Q44, Q45, Q46, Q47, Q48, Q49, Q50, Q51, Q52]), "depth" : 3.17 * mm});
        }
        {
            var Q0;
            {var subQ0=sQuery(id+"F1.wireOp",EDGE,"E34.2");var subQ1=sQuery(id+"F1.wireOp",EDGE,"E18");var subQ2=makeQuery(id+"F1.imprint","INTERSECT",VERTEX,{"derivedFrom":[subQ1,subQ0]});Q0=makeQuery(id+"F1.imprint","IMPRINT",FACE,{"disambiguationData":[TD([[makeQuery(id+"F1.imprint","IMPRINT",EDGE,{"disambiguationData":[TD([[subQ2,-1.0]])],"derivedFrom":subQ1}),-1.0]])]});}
            var Q1;
            {var subQ0=sQuery(id+"F1.wireOp",EDGE,"E34.3");var subQ1=sQuery(id+"F1.wireOp",EDGE,"E13");var subQ2=makeQuery(id+"F1.imprint","INTERSECT",VERTEX,{"derivedFrom":[subQ1,subQ0]});Q1=makeQuery(id+"F1.imprint","IMPRINT",FACE,{"disambiguationData":[TD([[makeQuery(id+"F1.imprint","IMPRINT",EDGE,{"disambiguationData":[TD([[subQ2,-1.0]])],"derivedFrom":subQ1}),1.0]])]});}
            var Q2;
            {var subQ0=sQuery(id+"F1.wireOp",EDGE,"E28");var subQ1=sQuery(id+"F1.wireOp",EDGE,"E18");var subQ2=makeQuery(id+"F1.imprint","INTERSECT",VERTEX,{"derivedFrom":[subQ1,subQ0]});Q2=makeQuery(id+"F1.imprint","IMPRINT",FACE,{"disambiguationData":[TD([[makeQuery(id+"F1.imprint","IMPRINT",EDGE,{"disambiguationData":[TD([[subQ2,-1.0]])],"derivedFrom":subQ1}),-1.0]])]});}
            var Q3;
            {var subQ5=sQuery(id+"F1.wireOp",EDGE,"E13");var subQ7=sQuery(id+"F1.wireOp",EDGE,"E35.5");var subQ9=makeQuery(id+"F1.imprint","INTERSECT",VERTEX,{"derivedFrom":[subQ5,subQ7]});Q3=makeQuery(id+"F1.imprint","IMPRINT",FACE,{"disambiguationData":[TD([[makeQuery(id+"F1.imprint","IMPRINT",EDGE,{"disambiguationData":[TD([[subQ9,1.0]])],"derivedFrom":subQ5}),1.0]])]});}
            var Q4;
            {var subQ0=sQuery(id+"F1.wireOp",EDGE,"E35.3");var subQ1=sQuery(id+"F1.wireOp",EDGE,"E26");var subQ2=makeQuery(id+"F1.imprint","INTERSECT",VERTEX,{"derivedFrom":[subQ1,subQ0]});Q4=makeQuery(id+"F1.imprint","IMPRINT",FACE,{"disambiguationData":[TD([[makeQuery(id+"F1.imprint","IMPRINT",EDGE,{"disambiguationData":[TD([[subQ2,-1.0]])],"derivedFrom":subQ1}),1.0]])]});}
            var Q5;
            {var subQ0=sQuery(id+"F1.wireOp",EDGE,"E35.3");var subQ1=sQuery(id+"F1.wireOp",EDGE,"E20");var subQ2=makeQuery(id+"F1.imprint","INTERSECT",VERTEX,{"derivedFrom":[subQ1,subQ0]});Q5=makeQuery(id+"F1.imprint","IMPRINT",FACE,{"disambiguationData":[TD([[makeQuery(id+"F1.imprint","IMPRINT",EDGE,{"disambiguationData":[TD([[subQ2,-1.0]])],"derivedFrom":subQ1}),-1.0]])]});}
            var Q6;
            {var subQ0=sQuery(id+"F1.wireOp",EDGE,"E36.0");var subQ1=sQuery(id+"F1.wireOp",EDGE,"E20");var subQ2=makeQuery(id+"F1.imprint","INTERSECT",VERTEX,{"derivedFrom":[subQ1,subQ0]});Q6=makeQuery(id+"F1.imprint","IMPRINT",FACE,{"disambiguationData":[TD([[makeQuery(id+"F1.imprint","IMPRINT",EDGE,{"disambiguationData":[TD([[subQ2,-1.0]])],"derivedFrom":subQ1}),-1.0]])]});}
            var Q7;
            {var subQ0=sQuery(id+"F1.wireOp",EDGE,"E36.0");var subQ1=sQuery(id+"F1.wireOp",EDGE,"E18");var subQ2=makeQuery(id+"F1.imprint","INTERSECT",VERTEX,{"derivedFrom":[subQ1,subQ0]});Q7=makeQuery(id+"F1.imprint","IMPRINT",FACE,{"disambiguationData":[TD([[makeQuery(id+"F1.imprint","IMPRINT",EDGE,{"disambiguationData":[TD([[subQ2,1.0]])],"derivedFrom":subQ1}),-1.0]])]});}
            var Q8;
            {var subQ5=sQuery(id+"F1.wireOp",EDGE,"E38.0");Q8=makeQuery(id+"F1.imprint","IMPRINT",FACE,{"disambiguationData":[TD([[makeQuery(id+"F1.imprint","IMPRINT",EDGE,{"derivedFrom":subQ5}),1.0]])]});}
            extrude(context, id + "F3", {"entities" : qUnion([Q0, Q1, Q2, Q3, Q4, Q5, Q6, Q7, Q8]), "depth" : 3.17 * mm});
        }
        {
            var Q0;
            {var subQ0=sQuery(id+"F1.wireOp",EDGE,"E34.4");var subQ1=sQuery(id+"F1.wireOp",EDGE,"E22");var subQ2=makeQuery(id+"F1.imprint","INTERSECT",VERTEX,{"derivedFrom":[subQ1,subQ0]});Q0=makeQuery(id+"F1.imprint","IMPRINT",FACE,{"disambiguationData":[TD([[makeQuery(id+"F1.imprint","IMPRINT",EDGE,{"disambiguationData":[TD([[subQ2,-1.0]])],"derivedFrom":subQ1}),1.0]])]});}
            var Q1;
            {var subQ0=sQuery(id+"F1.wireOp",EDGE,"E32");var subQ1=sQuery(id+"F1.wireOp",EDGE,"E24");var subQ2=makeQuery(id+"F1.imprint","INTERSECT",VERTEX,{"derivedFrom":[subQ1,subQ0]});Q1=makeQuery(id+"F1.imprint","IMPRINT",FACE,{"disambiguationData":[TD([[makeQuery(id+"F1.imprint","IMPRINT",EDGE,{"disambiguationData":[TD([[subQ2,-1.0]])],"derivedFrom":subQ1}),1.0]])]});}
            var Q2;
            {var subQ0=sQuery(id+"F1.wireOp",EDGE,"E35.0");var subQ1=sQuery(id+"F1.wireOp",EDGE,"E24");var subQ2=makeQuery(id+"F1.imprint","INTERSECT",VERTEX,{"derivedFrom":[subQ1,subQ0]});Q2=makeQuery(id+"F1.imprint","IMPRINT",FACE,{"disambiguationData":[TD([[makeQuery(id+"F1.imprint","IMPRINT",EDGE,{"disambiguationData":[TD([[subQ2,1.0]])],"derivedFrom":subQ1}),1.0]])]});}
            var Q3;
            {var subQ0=sQuery(id+"F1.wireOp",EDGE,"E35.0");var subQ1=sQuery(id+"F1.wireOp",EDGE,"E24");var subQ2=makeQuery(id+"F1.imprint","INTERSECT",VERTEX,{"derivedFrom":[subQ1,subQ0]});Q3=makeQuery(id+"F1.imprint","IMPRINT",FACE,{"disambiguationData":[TD([[makeQuery(id+"F1.imprint","IMPRINT",EDGE,{"disambiguationData":[TD([[subQ2,1.0]])],"derivedFrom":subQ1}),1.0]])]});}
            var Q4;
            {var subQ0=sQuery(id+"F1.wireOp",EDGE,"E34.4");var subQ1=sQuery(id+"F1.wireOp",EDGE,"E22");var subQ2=makeQuery(id+"F1.imprint","INTERSECT",VERTEX,{"derivedFrom":[subQ1,subQ0]});Q4=makeQuery(id+"F1.imprint","IMPRINT",FACE,{"disambiguationData":[TD([[makeQuery(id+"F1.imprint","IMPRINT",EDGE,{"disambiguationData":[TD([[subQ2,-1.0]])],"derivedFrom":subQ1}),1.0]])]});}
            var Q5;
            {var subQ0=sQuery(id+"F1.wireOp",EDGE,"E30");var subQ1=sQuery(id+"F1.wireOp",EDGE,"E22");var subQ2=makeQuery(id+"F1.imprint","INTERSECT",VERTEX,{"derivedFrom":[subQ1,subQ0]});Q5=makeQuery(id+"F1.imprint","IMPRINT",FACE,{"disambiguationData":[TD([[makeQuery(id+"F1.imprint","IMPRINT",EDGE,{"disambiguationData":[TD([[subQ2,-1.0]])],"derivedFrom":subQ1}),1.0]])]});}
            var Q6;
            {var subQ0=sQuery(id+"F1.wireOp",EDGE,"E34.1");var subQ1=sQuery(id+"F1.wireOp",EDGE,"E26");var subQ2=makeQuery(id+"F1.imprint","INTERSECT",VERTEX,{"derivedFrom":[subQ1,subQ0]});Q6=makeQuery(id+"F1.imprint","IMPRINT",FACE,{"disambiguationData":[TD([[makeQuery(id+"F1.imprint","IMPRINT",EDGE,{"disambiguationData":[TD([[subQ2,-1.0]])],"derivedFrom":subQ1}),1.0]])]});}
            var Q7;
            {var subQ5=sQuery(id+"F1.wireOp",EDGE,"E20");var subQ6=sQuery(id+"F1.wireOp",EDGE,"E15");var subQ7=makeQuery(id+"F1.imprint","INTERSECT",VERTEX,{"derivedFrom":[subQ6,subQ5]});Q7=makeQuery(id+"F1.imprint","IMPRINT",FACE,{"disambiguationData":[TD([[makeQuery(id+"F1.imprint","IMPRINT",EDGE,{"disambiguationData":[TD([[subQ7,-1.0]])],"derivedFrom":subQ6}),1.0]])]});}
            var Q8;
            {var subQ0=sQuery(id+"F1.wireOp",EDGE,"E35.5");var subQ1=sQuery(id+"F1.wireOp",EDGE,"E15");var subQ2=makeQuery(id+"F1.imprint","INTERSECT",VERTEX,{"derivedFrom":[subQ1,subQ0]});Q8=makeQuery(id+"F1.imprint","IMPRINT",FACE,{"disambiguationData":[TD([[makeQuery(id+"F1.imprint","IMPRINT",EDGE,{"disambiguationData":[TD([[subQ2,-1.0]])],"derivedFrom":subQ1}),1.0]])]});}
            var Q9;
            {var subQ0=sQuery(id+"F1.wireOp",EDGE,"E28");var subQ1=sQuery(id+"F1.wireOp",EDGE,"E15");var subQ2=makeQuery(id+"F1.imprint","INTERSECT",VERTEX,{"derivedFrom":[subQ1,subQ0]});Q9=makeQuery(id+"F1.imprint","IMPRINT",FACE,{"disambiguationData":[TD([[makeQuery(id+"F1.imprint","IMPRINT",EDGE,{"disambiguationData":[TD([[subQ2,-1.0]])],"derivedFrom":subQ1}),1.0]])]});}
            var Q10;
            {var subQ0=sQuery(id+"F1.wireOp",EDGE,"E28");var subQ1=sQuery(id+"F1.wireOp",EDGE,"E15");var subQ2=makeQuery(id+"F1.imprint","INTERSECT",VERTEX,{"derivedFrom":[subQ1,subQ0]});Q10=makeQuery(id+"F1.imprint","IMPRINT",FACE,{"disambiguationData":[TD([[makeQuery(id+"F1.imprint","IMPRINT",EDGE,{"disambiguationData":[TD([[subQ2,-1.0]])],"derivedFrom":subQ1}),1.0]])]});}
            var Q11;
            {var subQ1=sQuery(id+"F1.wireOp",EDGE,"E22");var subQ6=sQuery(id+"F1.wireOp",EDGE,"E35.0");var subQ11=makeQuery(id+"F1.imprint","INTERSECT",VERTEX,{"derivedFrom":[subQ1,subQ6]});Q11=makeQuery(id+"F1.imprint","IMPRINT",FACE,{"disambiguationData":[TD([[makeQuery(id+"F1.imprint","IMPRINT",EDGE,{"disambiguationData":[TD([[subQ11,-1.0]])],"derivedFrom":subQ1}),1.0]])]});}
            var Q12;
            {var subQ0=sQuery(id+"F1.wireOp",EDGE,"E30");var subQ1=sQuery(id+"F1.wireOp",EDGE,"E28");var subQ2=makeQuery(id+"F1.imprint","INTERSECT",VERTEX,{"derivedFrom":[subQ1,subQ0]});Q12=makeQuery(id+"F1.imprint","IMPRINT",FACE,{"disambiguationData":[TD([[makeQuery(id+"F1.imprint","IMPRINT",EDGE,{"disambiguationData":[TD([[subQ2,-1.0]])],"derivedFrom":subQ1}),1.0]])]});}
            var Q13;
            {var subQ0=sQuery(id+"F1.wireOp",EDGE,"E35.2");var subQ1=sQuery(id+"F1.wireOp",EDGE,"E34.1");var subQ2=makeQuery(id+"F1.imprint","INTERSECT",VERTEX,{"derivedFrom":[subQ1,subQ0]});Q13=makeQuery(id+"F1.imprint","IMPRINT",FACE,{"disambiguationData":[TD([[makeQuery(id+"F1.imprint","IMPRINT",EDGE,{"disambiguationData":[TD([[subQ2,1.0]])],"derivedFrom":subQ1}),1.0]])]});}
            var Q14;
            {var subQ0=sQuery(id+"F1.wireOp",EDGE,"E35.5");var subQ1=sQuery(id+"F1.wireOp",EDGE,"E34.0");var subQ2=makeQuery(id+"F1.imprint","INTERSECT",VERTEX,{"derivedFrom":[subQ1,subQ0]});Q14=makeQuery(id+"F1.imprint","IMPRINT",FACE,{"disambiguationData":[TD([[makeQuery(id+"F1.imprint","IMPRINT",EDGE,{"disambiguationData":[TD([[subQ2,-1.0]])],"derivedFrom":subQ1}),-1.0]])]});}
            var Q15;
            {var subQ0=sQuery(id+"F1.wireOp",EDGE,"E34.1");var subQ1=sQuery(id+"F1.wireOp",EDGE,"E24");var subQ2=makeQuery(id+"F1.imprint","INTERSECT",VERTEX,{"derivedFrom":[subQ1,subQ0]});Q15=makeQuery(id+"F1.imprint","IMPRINT",FACE,{"disambiguationData":[TD([[makeQuery(id+"F1.imprint","IMPRINT",EDGE,{"disambiguationData":[TD([[subQ2,-1.0]])],"derivedFrom":subQ1}),1.0]])]});}
            extrude(context, id + "F4", {"entities" : qUnion([Q0, Q1, Q2, Q3, Q4, Q5, Q6, Q7, Q8, Q9, Q10, Q11, Q12, Q13, Q14, Q15]), "depth" : 3.17 * mm});
        }
        {
            var Q0;
            Q0=qCreatedBy(makeId("Top.planeOp"),FACE);
            var sketch = newSketch(context, id + "F5", { "sketchPlane" : qUnion([Q0])});
            skLineSegment(sketch, "E39.0", {"start": v(66.11, 6.05) * mm, "end": v(66.11, -52.37) * mm});
            skFitSpline(sketch, "E39.1", {"points": [v(52.67, -51.16) * mm, v(64.82, -54.87) * mm, v(80.4, -50.58) * mm, v(85.16, -44.23) * mm]});
            skLineSegment(sketch, "E39.2", {"start": v(52.67, -51.16) * mm, "end": v(-83.6, -9.5) * mm});
            skArc(sketch, "E39.3", {"start": v(-52.81, 15.65) * mm, "mid": v(-91.73, 31.87) * mm, "end": v(-83.6, -9.5) * mm});
            skFitSpline(sketch, "E39.4", {"points": [v(-52.81, 15.65) * mm, v(12.06, 14.43) * mm, v(24.52, 13.11) * mm, v(11.95, 42.23) * mm]});
            skArc(sketch, "E39.5", {"start": v(17.17, 35.44) * mm, "mid": v(15.59, 35.73) * mm, "end": v(14.99, 34.24) * mm});
            skArc(sketch, "E39.6", {"start": v(17.17, 35.44) * mm, "mid": v(39.22, 16.71) * mm, "end": v(66.11, 6.05) * mm});
            skCircle(sketch, "E40.0", {"center": v(-60.76, -4.74) * mm, "radius": 5.04 * mm});
            skCircle(sketch, "E40.1", {"center": v(-37.42, -11.87) * mm, "radius": 5.04 * mm});
            skCircle(sketch, "E40.2", {"center": v(-14.07, -19.01) * mm, "radius": 5.04 * mm});
            skCircle(sketch, "E40.3", {"center": v(9.27, -26.15) * mm, "radius": 5.04 * mm});
            skCircle(sketch, "E40.4", {"center": v(32.61, -33.28) * mm, "radius": 5.04 * mm});
            skCircle(sketch, "E40.5", {"center": v(55.95, -40.42) * mm, "radius": 5.04 * mm});
            skSolve(sketch);
        }
        {
            var Q0;
            Q0=makeQuery(id+"F5.imprint","IMPRINT",FACE,{"disambiguationData":[TD([[makeQuery(id+"F5.imprint","IMPRINT",EDGE,{"derivedFrom":sQuery(id+"F5.wireOp",EDGE,"E40.0")}),1.0]])]});
            var Q1;
            Q1=makeQuery(id+"F5.imprint","IMPRINT",FACE,{"disambiguationData":[TD([[makeQuery(id+"F5.imprint","IMPRINT",EDGE,{"derivedFrom":sQuery(id+"F5.wireOp",EDGE,"E40.1")}),1.0]])]});
            var Q2;
            Q2=makeQuery(id+"F5.imprint","IMPRINT",FACE,{"disambiguationData":[TD([[makeQuery(id+"F5.imprint","IMPRINT",EDGE,{"derivedFrom":sQuery(id+"F5.wireOp",EDGE,"E40.2")}),1.0]])]});
            var Q3;
            Q3=makeQuery(id+"F5.imprint","IMPRINT",FACE,{"disambiguationData":[TD([[makeQuery(id+"F5.imprint","IMPRINT",EDGE,{"derivedFrom":sQuery(id+"F5.wireOp",EDGE,"E40.3")}),1.0]])]});
            var Q4;
            Q4=makeQuery(id+"F5.imprint","IMPRINT",FACE,{"disambiguationData":[TD([[makeQuery(id+"F5.imprint","IMPRINT",EDGE,{"derivedFrom":sQuery(id+"F5.wireOp",EDGE,"E40.4")}),1.0]])]});
            var Q5;
            Q5=makeQuery(id+"F5.imprint","IMPRINT",FACE,{"disambiguationData":[TD([[makeQuery(id+"F5.imprint","IMPRINT",EDGE,{"derivedFrom":sQuery(id+"F5.wireOp",EDGE,"E40.5")}),1.0]])]});
            extrude(context, id + "F6", {"entities" : qUnion([Q0, Q1, Q2, Q3, Q4, Q5]), "operationType" : NewBodyOperationType.REMOVE, "endBound" : BoundingType.THROUGH_ALL, "depth" : 25.4 * mm});
        }
        {
            var Q0;
            Q0=makeQuery(id+"F4.opExtrude","SWEPT_EDGE",EDGE,{"disambiguationData":[OSD([sQuery(id+"F1.wireOp",EDGE,"E35.1"),sQuery(id+"F1.wireOp",EDGE,"E35.2")])]});
            fillet(context, id + "F7", {"entities" : qUnion([Q0]), "radius" : 1.27 * mm, "tangentPropagation" : true, "allowEdgeOverflow" : false});
        }
        {
            var Q0;
            Q0=qCreatedBy(makeId("Top.planeOp"),FACE);
            var sketch = newSketch(context, id + "F8", { "sketchPlane" : qUnion([Q0])});
            skLineSegment(sketch, "E41.0", {"start": v(-68.45, -21.17) * mm, "end": v(61.8, -21.17) * mm, "construction": true});
            skLineSegment(sketch, "E41.1", {"start": v(-91.8, 9.52) * mm, "end": v(75.82, 9.52) * mm, "construction": true});
            skLineSegment(sketch, "E42.bottom", {"start": v(35.79, -16.14) * mm, "end": v(29.44, -16.14) * mm});
            skLineSegment(sketch, "E42.top", {"start": v(35.79, -9.79) * mm, "end": v(29.44, -9.79) * mm});
            skLineSegment(sketch, "E42.left", {"start": v(35.79, -16.14) * mm, "end": v(35.79, -9.79) * mm});
            skLineSegment(sketch, "E42.right", {"start": v(29.44, -16.14) * mm, "end": v(29.44, -9.79) * mm});
            skPoint(sketch, "E42.middle", {"position": v(32.61, -12.96) * mm});
            skLineSegment(sketch, "E43.0", {"start": v(62.7, -4.76) * mm, "end": v(-45.1, -4.76) * mm, "construction": true});
            skLineSegment(sketch, "E44", {"start": v(32.61, -12.96) * mm, "end": v(18.74, -12.96) * mm, "construction": true});
            skPoint(sketch, "E45", {"position": v(32.61, -33.28) * mm});
            skSolve(sketch);
        }
        {
            var Q0;
            Q0=qSketchRegion(id+"F8",true);
            extrude(context, id + "F9", {"entities" : qUnion([Q0]), "operationType" : NewBodyOperationType.REMOVE, "depth" : 25.4 * mm});
        }
    });
